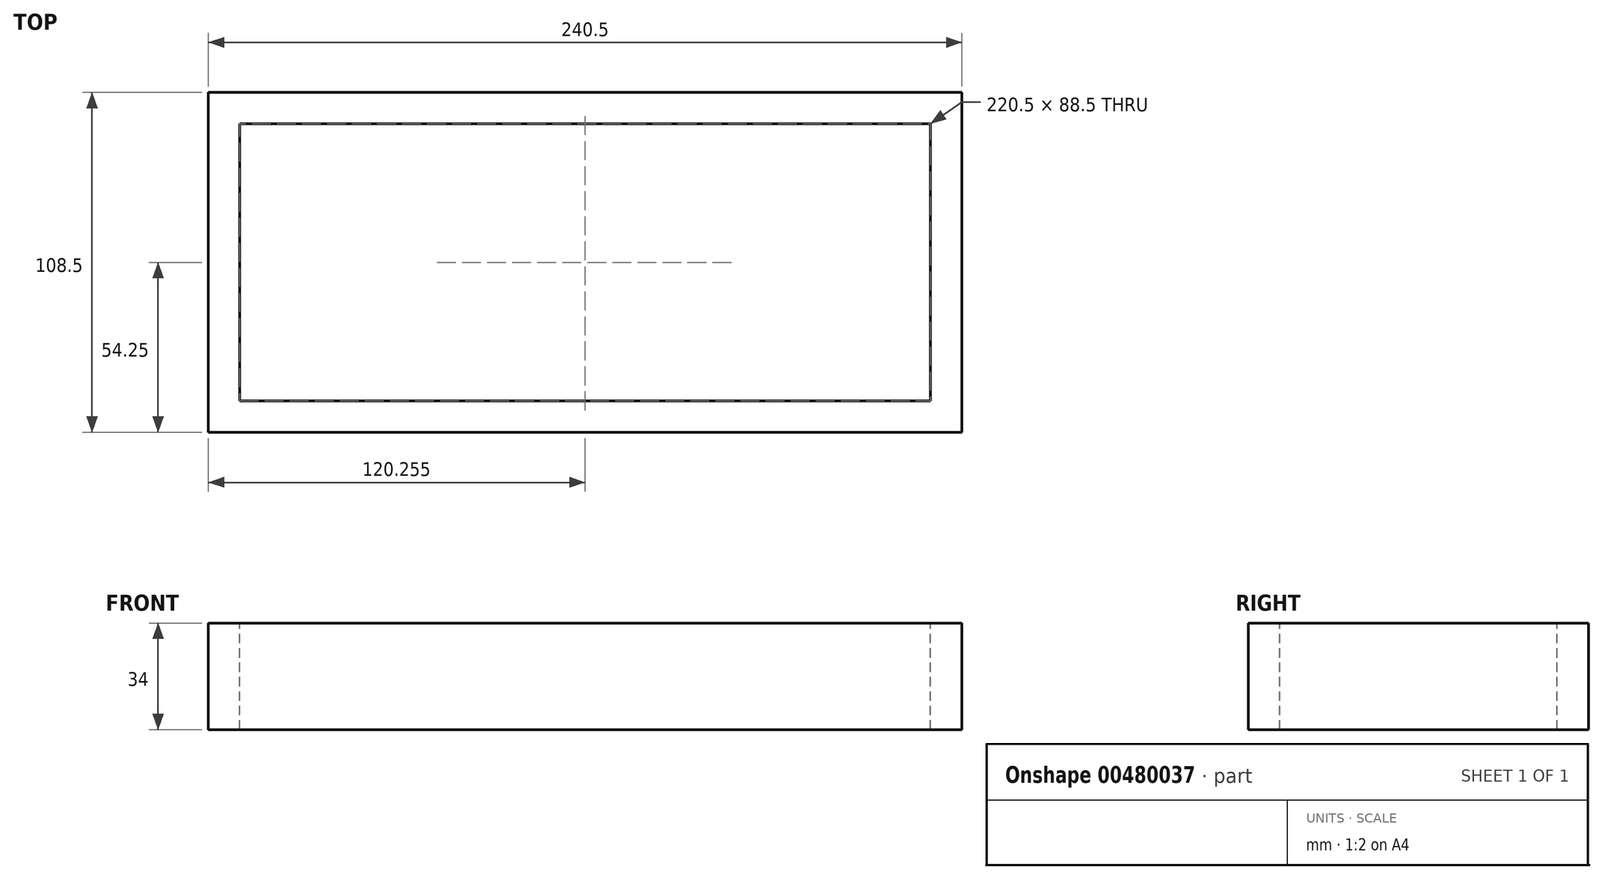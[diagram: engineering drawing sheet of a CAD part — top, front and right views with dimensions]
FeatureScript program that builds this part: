
annotation { "Feature Type Name" : "Feature", "Feature Type Description" : "" }
export const myFeature = defineFeature(function(context is Context, id is Id, definition is map)
    precondition{}
    {
        {
            var Q0;
            Q0=qCreatedBy(makeId("Top.planeOp"),FACE);
            var sketch = newSketch(context, id + "F0", { "sketchPlane" : qUnion([Q0])});
            skLineSegment(sketch, "E0.bottom", {"start": v(-150, 73.27) * mm, "end": v(90.5, 73.27) * mm});
            skLineSegment(sketch, "E0.top", {"start": v(-150, -35.23) * mm, "end": v(90.5, -35.23) * mm});
            skLineSegment(sketch, "E0.left", {"start": v(-150, 73.27) * mm, "end": v(-150, -35.23) * mm});
            skLineSegment(sketch, "E0.right", {"start": v(90.5, 73.27) * mm, "end": v(90.5, -35.23) * mm});
            skSolve(sketch);
        }
        {
            var Q0;
            Q0=qSketchRegion(id+"F0",true);
            extrude(context, id + "F1", {"entities" : qUnion([Q0]), "depth" : 34 * mm});
        }
        {
            var Q0;
            Q0=makeQuery(id+"F1.opExtrude","CAP_FACE",FACE,{"disambiguationData":[OSD([sQuery(id+"F0.wireOp",EDGE,"E0.bottom"),sQuery(id+"F0.wireOp",EDGE,"E0.top"),sQuery(id+"F0.wireOp",EDGE,"E0.left"),sQuery(id+"F0.wireOp",EDGE,"E0.right")])],"isStart":false});
            var sketch = newSketch(context, id + "F2", { "sketchPlane" : qUnion([Q0])});
            skLineSegment(sketch, "E1", {"start": v(-150, 73.27) * mm, "end": v(90.5, -35.23) * mm, "construction": true});
            skLineSegment(sketch, "E2", {"start": v(-29.75, 19.02) * mm, "end": v(-29.75, 63.27) * mm, "construction": true});
            skLineSegment(sketch, "E3", {"start": v(-29.75, 19.02) * mm, "end": v(-29.75, -25.23) * mm, "construction": true});
            skLineSegment(sketch, "E4", {"start": v(80.5, -25.23) * mm, "end": v(80.5, 63.27) * mm});
            skLineSegment(sketch, "E5", {"start": v(-140, -25.23) * mm, "end": v(-140, 63.27) * mm});
            skLineSegment(sketch, "E6", {"start": v(80.5, -25.23) * mm, "end": v(-140, -25.23) * mm});
            skLineSegment(sketch, "E7", {"start": v(80.5, 63.27) * mm, "end": v(-140, 63.27) * mm});
            skSolve(sketch);
        }
        {
            var Q0;
            Q0=qSketchRegion(id+"F2",true);
            extrude(context, id + "F3", {"entities" : qUnion([Q0]), "operationType" : NewBodyOperationType.REMOVE, "oppositeDirection" : true, "depth" : 34 * mm});
        }
    });
